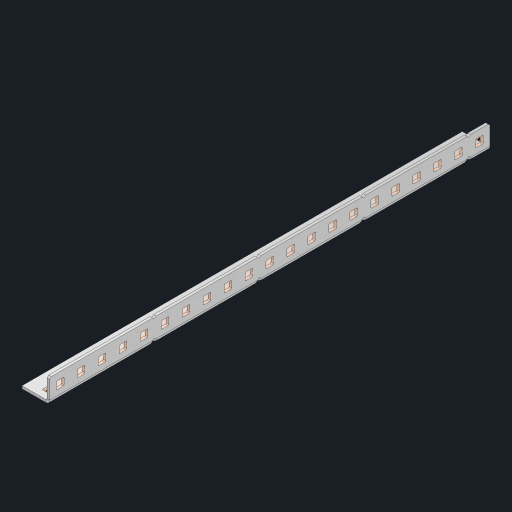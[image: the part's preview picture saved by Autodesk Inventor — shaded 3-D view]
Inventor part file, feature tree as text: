
AUTODESK INVENTOR PART (.ipt)
format: ipt  version: 2023 (Build 270158000, 158)  size: 798,208 bytes
history: native  units: in
note: dims shown in document units (in); Inventor stores cm internally (conversion verified against a paired STEP export)
features: other x47, extrude x41, sheet_metal_op x10, sketch x8, mirror x1, pattern_linear x1, chamfer x1
ambient origin geometry x8: Origin, YZ Plane, XZ Plane, XY Plane, X Axis, Y Axis, Z Axis, Center Point
bodies: Solid1 (feature_tree), Body (feature_tree)
feature tree (109):
  other  "Flange Pattern Plane"
  sheet_metal_op  "Flange Pattern"
  sheet_metal_op  "Body Pattern"
  other  "Arc Length"
  mirror  "Notch Mirror"
  pattern_linear  "Notch Pattern"  Spacing1=0.25in  [1 undecoded]
  chamfer  "End Chamfer"
  extrude  "Half Cut"  Depth=0.0625in
  sketch  "Sketch1"  dims[d0=1.5in]
  other  "Plate1"
  sketch  "Sketch2"  dims[d1=10.5in]
  other  "Plate2"
  sheet_metal_op  "Bend1"
  sheet_metal_op  "Corner1"
  sketch  "Sketch3"  dims[d2=0.0625in]
  other  "Flange Pattern Sketch"
  sketch  "Sketch7"  dims[d3=0.0625in]
  other  "Srf1"
  other  "Srf2"
  sketch  "Sketch8"  dims[d4=0.0312in]
  sketch  "Sketch9"  dims[d5=0.125in]
  other  "Srf91"
  sheet_metal_op  "Body Pattern Sketch"
  other  "Srf92"
  sketch  "Sketch13"  dims[d6=0.0625in]
  sketch  "Sketch14"  dims[d7=0.5in d8=90.0deg d9=0.0312in d10=0.25in d11=0.0625in d12=0.0625in d16=0.182in d17=0.02in d18=0.0625in d19=0.0in d20=0.25in d21=0.25in d46=0.172in d47=1.0in d48=0.0in d49=0.182in d50=0.02in d51=0.25in d52=0.25in d53=0.0625in d54=0.0in d55=0.172in d56=1.0in d57=0.0in d60=8.2677in d62=0.5in d63=0.3937in d65=0.5in d85=0.1473in d86=0.1782in d88=0.04in d89=0.0625in d90=0.0in d91=0.04in d92=0.0491in d95=2.5in d96=0.04in d97=0.25in d98=45.0deg d101=0.0in d102=2.497in d131=0.5in d132=8.2677in d134=0.5in d139=0.5in]
  other  "Srf856"
  other  "Srf1310"
  other  "Srf1311"
  other  "Srf1312"
  other  "Srf1376"
  other  "Srf1377"
  other  "Srf1728"
  other  "Srf1755"
  other  "Srf1878"
  other  "Srf1879"
  other  "Srf1880"
  other  "Srf1881"
  other  "Srf1882"
  other  "Srf1883"
  other  "Srf1884"
  other  "Srf1885"
  other  "Srf1886"
  other  "Srf1887"
  other  "Srf1888"
  other  "Srf1889"
  other  "Srf1890"
  other  "Srf1891"
  other  "Srf1892"
  other  "Srf1942"
  other  "Srf1943"
  other  "Srf1944"
  other  "Srf1945"
  other  "Srf1946"
  other  "Srf1947"
  other  "Srf1948"
  other  "Srf1949"
  other  "Srf1950"
  other  "Srf1951"
  other  "Srf1952"
  other  "Srf1953"
  other  "Srf1954"
  other  "Srf1955"
  other  "Srf1956"
  sheet_metal_op  "Flange Stamp"
  sheet_metal_op  "Flange Circle"
  sheet_metal_op  "Body Stamp"
  sheet_metal_op  "Body Circle"
  sheet_metal_op  "Notch"
  extrude  "ExtrusionSrf2"  Depth=0.0625in
  extrude  "ExtrusionSrf92"  Depth=0.5in
  extrude  "ExtrusionSrf856"  Depth=0.02in
  extrude  "ExtrusionSrf1310"  Depth=0.0625in
  extrude  "ExtrusionSrf1311"  TaperAngle=0.0deg  [1 undecoded]
  extrude  "ExtrusionSrf1312"  Depth=0.5in
  extrude  "ExtrusionSrf1376"  Depth=0.5in
  extrude  "ExtrusionSrf1377"  Depth=0.5in
  extrude  "ExtrusionSrf1728"  Depth=0.5in TaperAngle=0.0deg
  extrude  "ExtrusionSrf1755"  Depth=0.5in
  extrude  "ExtrusionSrf1878"  Depth=0.02in
  extrude  "ExtrusionSrf1879"  Depth=0.5in
  extrude  "ExtrusionSrf1880"  Depth=0.5in
  extrude  "ExtrusionSrf1881"  Depth=0.0625in
  extrude  "ExtrusionSrf1882"  TaperAngle=0.0deg  [1 undecoded]
  extrude  "ExtrusionSrf1883"  Depth=0.5in
  extrude  "ExtrusionSrf1884"  Depth=0.5in TaperAngle=0.0deg
  extrude  "ExtrusionSrf1885"  Depth=0.5in
  extrude  "ExtrusionSrf1886"  Depth=0.5in
  extrude  "ExtrusionSrf1887"  Depth=0.5in
  extrude  "ExtrusionSrf1888"  Depth=0.5in
  extrude  "ExtrusionSrf1889"  Depth=0.5in
  extrude  "ExtrusionSrf1890"  Depth=0.0625in
  extrude  "ExtrusionSrf1891"  TaperAngle=0.0deg  [1 undecoded]
  extrude  "ExtrusionSrf1892"  Depth=0.5in
  extrude  "ExtrusionSrf1942"  Depth=0.5in
  extrude  "ExtrusionSrf1943"  Depth=0.5in
  extrude  "ExtrusionSrf1944"  Depth=0.5in TaperAngle=45.0deg
  extrude  "ExtrusionSrf1945"  TaperAngle=0.0deg  [1 undecoded]
  extrude  "ExtrusionSrf1946"  Depth=0.5in
  extrude  "ExtrusionSrf1947"  Depth=0.5in
  extrude  "ExtrusionSrf1948"  Depth=0.5in
  extrude  "ExtrusionSrf1949"  Depth=0.5in
  extrude  "ExtrusionSrf1950"  Depth=0.5in
  extrude  "ExtrusionSrf1951"  [1 undecoded]
  extrude  "ExtrusionSrf1952"  [1 undecoded]
  extrude  "ExtrusionSrf1953"  [1 undecoded]
  extrude  "ExtrusionSrf1954"  [1 undecoded]
  extrude  "ExtrusionSrf1955"  [1 undecoded]
  extrude  "ExtrusionSrf1956"  [1 undecoded]
note: 11 required parameter values undecoded (feature->parameter linkage not recoverable at this tier; creation-order binding heuristic only, values carry confidence <= 0.55)
